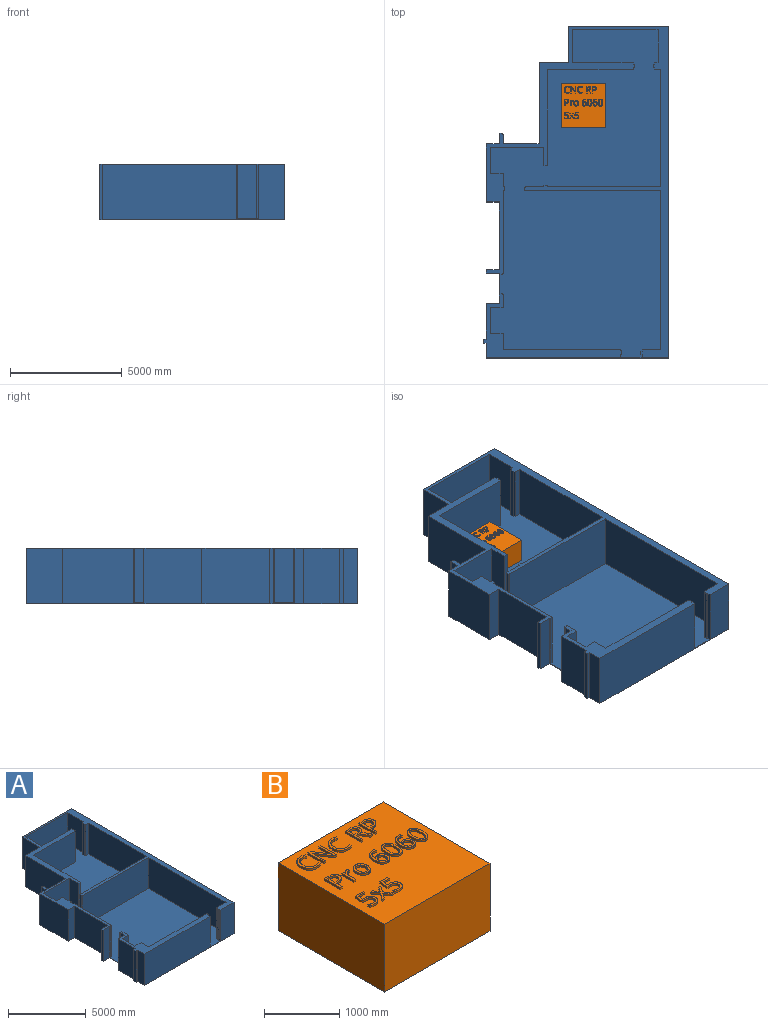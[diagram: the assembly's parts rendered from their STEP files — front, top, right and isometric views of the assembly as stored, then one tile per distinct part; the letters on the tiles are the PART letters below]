
ASSEMBLY  parts=2 mates=1
PART A: 99 faces, bbox 8276.1x14831.1x2468.9 mm
  f0: plane 14664.87x7617.86mm, normal (0,0,1), area 87596597.3mm2, adj f1,f13,f14,f22,f23,f24,f25,f26
  f1: plane 8150.75x2468.88mm, normal (0,-1,0), area 17745459.7mm2, adj f0,f2,f20,f21,f22,f38,f97,f98
  f2: plane 14831.13x2468.88mm, normal (1,0,0), area 36616275.6mm2, adj f1,f3,f21,f98
  f3: plane 4488.1x2468.88mm, normal (0,1,0), area 11080584.4mm2, adj f2,f4,f21,f98
  f4: plane 2468.88x1621.95mm, normal (-1,0,0), area 4004402.6mm2, adj f3,f5,f21,f98
  f5: plane 2468.88x1301.63mm, normal (0,1,0), area 3213578.3mm2, adj f4,f6,f21,f98
  f6: plane 3647.91x2468.88mm, normal (-1,0,0), area 9006245.3mm2, adj f5,f7,f21,f98
  f7: plane 2468.88x2348.04mm, normal (0,1,0), area 5391615mm2, adj f6,f8,f21,f39,f40,f46,f98
  f8: plane 2590.65x2468.88mm, normal (-1,0,0), area 6395991.8mm2, adj f7,f9,f21,f98
  f9: plane 2468.88x577.86mm, normal (0,-1,0), area 1426664.6mm2, adj f8,f10,f21,f98
  f10: plane 3026.45x2468.88mm, normal (-1,0,0), area 7471946.9mm2, adj f9,f11,f21,f98
  f11: plane 2468.88x577.86mm, normal (0,1,0), area 1426664.6mm2, adj f10,f12,f21,f98
  f12: plane 2468.88x156.95mm, normal (-1,0,0), area 387486mm2, adj f11,f13,f21,f98
  f13: plane 2468.88x603.36mm, normal (0,-1,0), area 1488839.6mm2, adj f0,f12,f14,f21,f47,f98
  f14: plane 2468.88x1372.56mm, normal (-1,0,0), area 1021102.5mm2, adj f0,f13,f15,f21,f37,f38
  f15: plane 2468.88x586.51mm, normal (0,1,0), area 1448027.1mm2, adj f14,f16,f21,f38
  f16: plane 2468.88x1571.79mm, normal (-1,0,0), area 3880553.8mm2, adj f15,f17,f21,f38
  f17: plane 2468.88x129.53mm, normal (0,1,0), area 319783.6mm2, adj f16,f18,f21,f38
  f18: plane 2468.88x191.97mm, normal (-1,0,0), area 473943.5mm2, adj f17,f19,f21,f38
  f19: plane 2468.88x125.31mm, normal (0,-1,0), area 309366.7mm2, adj f18,f20,f21,f38
  f20: plane 2468.88x650.91mm, normal (-1,0,0), area 1607024.3mm2, adj f1,f19,f21,f38
  f21: plane 14831.13x8276.06mm, normal (0,0,-1), area 103714263.4mm2, adj f1,f2,f3,f4,f5,f6,f7,f8
  f22: plane 2438.4x173.04mm, normal (1,0,0), area 421945.8mm2, adj f0,f1,f23,f38
  f23: plane 2438.4x49.23mm, normal (0,-1,0), area 120036.9mm2, adj f0,f22,f24,f38
  f24: plane 2438.4x135.75mm, normal (1,0,0), area 331009.4mm2, adj f0,f23,f25,f38
  f25: plane 2438.4x37.29mm, normal (0,1,0), area 90924.1mm2, adj f0,f24,f26,f38
  f26: plane 2438.4x67.02mm, normal (1,0,0), area 163418mm2, adj f0,f25,f27,f38
  f27: plane 5244.59x2438.4mm, normal (0,1,0), area 12788415.3mm2, adj f0,f26,f28,f38
  f28: plane 2438.4x698.26mm, normal (1,0,0), area 1702637.3mm2, adj f0,f27,f29,f38
  f29: plane 2438.4x565.36mm, normal (0,1,0), area 1378581.8mm2, adj f0,f28,f30,f38
  f30: plane 2438.4x1164.09mm, normal (1,0,0), area 2838507mm2, adj f0,f29,f31,f38
  f31: plane 2438.4x565.36mm, normal (0,-1,0), area 1378581.8mm2, adj f0,f30,f32,f38
  f32: plane 2438.4x581.62mm, normal (1,0,0), area 1418221.9mm2, adj f0,f31,f33,f38
  f33: plane 2438.4x31.86mm, normal (0,1,0), area 77690.3mm2, adj f0,f32,f34,f38
  f34: plane 2438.4x41.25mm, normal (1,0,0), area 100572.6mm2, adj f0,f33,f35,f38
  f35: plane 2438.4x108.66mm, normal (0,1,0), area 264949.5mm2, adj f0,f34,f36,f38
  f36: plane 2438.4x44.75mm, normal (-1,0,0), area 109122.4mm2, adj f0,f35,f37,f38
  f37: plane 2438.4x25.61mm, normal (0,1,0), area 62436.6mm2, adj f0,f14,f36,f38
  f38: plane 6164.04x2861.02mm, normal (0,0,1), area 3232495.8mm2, adj f1,f14,f15,f16,f17,f18,f19,f20
  f39: plane 466.68x166.26mm, normal (0,0,-1), area 75215.3mm2, adj f7,f40,f41,f42,f43,f44,f45,f46
  f40: plane 2438.4x429.05mm, normal (1,0,0), area 1046190.8mm2, adj f7,f39,f41,f98
  f41: plane 2438.4x37.63mm, normal (0,1,0), area 91762.1mm2, adj f39,f40,f42,f98
  f42: plane 2438.4x37.63mm, normal (1,0,0), area 91761.8mm2, adj f39,f41,f43,f98
  f43: plane 2438.4x103.13mm, normal (0,1,0), area 251472.7mm2, adj f39,f42,f44,f98
  f44: plane 2438.4x37.63mm, normal (-1,0,0), area 91761.8mm2, adj f39,f43,f45,f98
  f45: plane 2438.4x25.5mm, normal (0,1,0), area 62178.2mm2, adj f39,f44,f46,f98
  f46: plane 2438.4x429.05mm, normal (-1,0,0), area 1046190.8mm2, adj f7,f39,f45,f98
  f47: plane 2438.4x46.41mm, normal (-1,0,0), area 113171.5mm2, adj f0,f13,f48,f98
  f48: plane 2438.4x103.37mm, normal (0,-1,0), area 252064mm2, adj f0,f47,f49,f98
  f49: plane 2438.4x44.3mm, normal (1,0,0), area 108027.3mm2, adj f0,f48,f50,f98
  f50: plane 2438.4x37.15mm, normal (0,-1,0), area 90575.9mm2, adj f0,f49,f51,f98
  f51: plane 3677.29x2438.4mm, normal (1,0,0), area 8966714.5mm2, adj f0,f50,f52,f98
  f52: plane 2438.4x61.68mm, normal (0,-1,0), area 150402.7mm2, adj f0,f51,f53,f98
  f53: plane 2438.4x182.72mm, normal (1,0,0), area 445546.1mm2, adj f0,f52,f54,f98
  f54: plane 2438.4x58.49mm, normal (0,1,0), area 142625.9mm2, adj f0,f53,f55,f98
  f55: plane 2438.4x586.03mm, normal (1,0,0), area 1428964.5mm2, adj f0,f54,f56,f98
  f56: plane 2438.4x571.23mm, normal (0,1,0), area 1392877.5mm2, adj f0,f55,f57,f98
  f57: plane 2438.4x1177.99mm, normal (1,0,0), area 2872409.6mm2, adj f0,f56,f58,f98
  f58: plane 2438.4x2388.44mm, normal (0,-1,0), area 5823964mm2, adj f0,f57,f59,f98
  f59: plane 2438.4x800.31mm, normal (-1,0,0), area 1951472.7mm2, adj f0,f58,f60,f98
  f60: plane 2438.4x173.35mm, normal (0,-1,0), area 422690.5mm2, adj f0,f59,f61,f98
  f61: plane 4263.95x2438.4mm, normal (1,0,0), area 10397204.9mm2, adj f0,f60,f62,f98
  f62: plane 3816.53x2438.4mm, normal (0,-1,0), area 9306235.4mm2, adj f0,f61,f63,f98
  f63: plane 2438.4x99.27mm, normal (1,0,0), area 242066.6mm2, adj f0,f62,f64,f98
  f64: plane 2438.4x49.67mm, normal (0,-1,0), area 121119.4mm2, adj f0,f63,f65,f98
  f65: plane 2438.4x156.11mm, normal (1,0,0), area 380662.8mm2, adj f0,f64,f66,f98
  f66: plane 2438.4x49.67mm, normal (0,1,0), area 121119.4mm2, adj f0,f65,f67,f98
  f67: plane 2438.4x81.01mm, normal (1,0,0), area 197536.8mm2, adj f0,f66,f68,f98
  f68: plane 2718.1x2438.4mm, normal (0,1,0), area 6627812.9mm2, adj f0,f67,f69,f98
  f69: plane 2438.4x1455.69mm, normal (1,0,0), area 3549555.4mm2, adj f0,f68,f70,f98
  f70: plane 3828.21x2438.4mm, normal (0,-1,0), area 9334704.6mm2, adj f0,f69,f71,f98
  f71: plane 2438.4x1462.38mm, normal (-1,0,0), area 3565873mm2, adj f0,f70,f72,f98
  f72: plane 2438.4x145.51mm, normal (0,1,0), area 354813.2mm2, adj f0,f71,f73,f98
  f73: plane 2438.4x74.32mm, normal (-1,0,0), area 181219.2mm2, adj f0,f72,f74,f98
  f74: plane 2438.4x50.83mm, normal (0,1,0), area 123950.6mm2, adj f0,f73,f75,f98
  f75: plane 2438.4x160.46mm, normal (-1,0,0), area 391262.2mm2, adj f0,f74,f76,f98
  f76: plane 2438.4x50.83mm, normal (0,-1,0), area 123950.6mm2, adj f0,f75,f77,f98
  f77: plane 2438.4x81.33mm, normal (-1,0,0), area 198320.5mm2, adj f0,f76,f78,f98
  f78: plane 2438.4x274.95mm, normal (0,-1,0), area 670431.2mm2, adj f0,f77,f79,f98
  f79: plane 5241.25x2438.4mm, normal (-1,0,0), area 12780253mm2, adj f0,f78,f80,f98
  f80: plane 5055.05x2438.4mm, normal (0,1,0), area 12326241.8mm2, adj f0,f79,f81,f98
  f81: plane 2438.4x45.1mm, normal (1,0,0), area 109968.3mm2, adj f0,f80,f82,f98
  f82: plane 2438.4x174.05mm, normal (0,1,0), area 424393.3mm2, adj f0,f81,f83,f98
  f83: plane 2438.4x45.1mm, normal (-1,0,0), area 109968.3mm2, adj f0,f82,f84,f98
  f84: plane 2438.4x813.8mm, normal (0,1,0), area 1984361.4mm2, adj f0,f83,f85,f98
  f85: plane 2438.4x9.07mm, normal (-1,0,0), area 22106.8mm2, adj f0,f84,f86,f98
  f86: plane 2438.4x39.18mm, normal (0,1,0), area 95532mm2, adj f0,f85,f87,f98
  f87: plane 2438.4x143mm, normal (-1,0,0), area 348695.6mm2, adj f0,f86,f88,f98
  f88: plane 2438.4x39.18mm, normal (0,-1,0), area 95532mm2, adj f0,f87,f89,f98
  f89: plane 2438.4x30.65mm, normal (-1,0,0), area 74743.8mm2, adj f0,f88,f90,f98
  f90: plane 6036.43x2438.4mm, normal (0,-1,0), area 14719237mm2, adj f0,f89,f91,f98
  f91: plane 7086.6x2438.4mm, normal (-1,0,0), area 17279965.4mm2, adj f0,f90,f92,f98
  f92: plane 2438.4x833.23mm, normal (0,1,0), area 2031756.8mm2, adj f0,f91,f93,f98
  f93: plane 2438.4x75.93mm, normal (-1,0,0), area 185138.2mm2, adj f0,f92,f94,f98
  f94: plane 2438.4x53.7mm, normal (0,1,0), area 130949mm2, adj f0,f93,f95,f98
  f95: plane 2438.4x152.9mm, normal (-1,0,0), area 372840.6mm2, adj f0,f94,f96,f98
  f96: plane 2438.4x51.36mm, normal (0,-1,0), area 125241mm2, adj f0,f95,f97,f98
  f97: plane 2438.4x146.98mm, normal (-1,0,0), area 358394.4mm2, adj f0,f1,f96,f98
  f98: plane 14831.13x8137.78mm, normal (0,0,1), area 12960385.6mm2, adj f1,f2,f3,f4,f5,f6,f7,f8
PART B: 284 faces, bbox 1981.2x2000.3x1132.2 mm
  f0: plane 2000.25x1981.2mm, normal (0,0,1), area 3493503.6mm2, adj f1,f2,f3,f4,f6,f7,f8,f9
  f1: plane 1981.2x1101.73mm, normal (0,1,0), area 2182737.6mm2, adj f0,f2,f4,f5
  f2: plane 2000.25x1101.73mm, normal (-1,0,0), area 2203725.4mm2, adj f0,f1,f3,f5
  f3: plane 1981.2x1101.73mm, normal (0,-1,0), area 2182737.6mm2, adj f0,f2,f4,f5
  f4: plane 2000.25x1101.73mm, normal (1,0,0), area 2203725.4mm2, adj f0,f1,f3,f5
  f5: plane 2000.25x1981.2mm, normal (0,0,-1), area 3962895.3mm2, adj f1,f2,f3,f4
  f6: extruded ~78.65x33.17mm, area 2688.6mm2, adj f0,f7,f20,f21
  f7: extruded ~68.66x30.48mm, area 2166.9mm2, adj f0,f6,f8,f21
  f8: plane 30.48x30.16mm, normal (0.9,-0.44,0), area 1025.2mm2, adj f0,f7,f9,f21
  f9: extruded ~83.08x30.48mm, area 2609.2mm2, adj f0,f8,f10,f21
  f10: extruded ~77.62x30.48mm, area 2464.4mm2, adj f0,f9,f11,f21
  f11: extruded ~54.14x50.44mm, area 2289.1mm2, adj f0,f10,f12,f21
  f12: extruded ~81.82x30.48mm, area 2573.1mm2, adj f0,f11,f13,f21
  f13: extruded ~115.16x36.28mm, area 3764.5mm2, adj f0,f12,f14,f21
  f14: extruded ~103.02x40.55mm, area 3482mm2, adj f0,f13,f15,f21
  f15: extruded ~77.52x30.48mm, area 2403mm2, adj f0,f14,f16,f21
  f16: plane 30.76x30.48mm, normal (1,0,0), area 937.5mm2, adj f0,f15,f17,f21
  f17: extruded ~72.17x30.48mm, area 2233.6mm2, adj f0,f16,f18,f21
  f18: extruded ~79.28x32.38mm, area 2697.9mm2, adj f0,f17,f19,f21
  f19: extruded ~91.65x30.48mm, area 2982mm2, adj f0,f18,f20,f21
  f20: extruded ~90.85x30.48mm, area 2969.8mm2, adj f0,f6,f19,f21
  f21: plane 310.69x228.6mm, normal (0,0,1), area 19972.9mm2, adj f6,f7,f8,f9,f10,f11,f12,f13
  f22: plane 40.08x30.48mm, normal (0,-1,0), area 1221.8mm2, adj f0,f23,f36,f37
  f23: plane 302.22x30.48mm, normal (1,0,0), area 9211.7mm2, adj f0,f22,f24,f37
  f24: plane 32.87x30.48mm, normal (0,1,0), area 1002mm2, adj f0,f23,f25,f37
  f25: plane 173.43x30.48mm, normal (-1,0,0), area 5286.3mm2, adj f0,f24,f26,f37
  f26: extruded ~43.33x30.48mm, area 1321.2mm2, adj f0,f25,f27,f37
  f27: extruded ~35.85x30.48mm, area 1094.2mm2, adj f0,f26,f28,f37
  f28: plane 30.48x1.65mm, normal (0,1,0), area 50.4mm2, adj f0,f27,f29,f37
  f29: plane 252.61x164.77mm, normal (0.84,0.55,0), area 9192.7mm2, adj f0,f28,f30,f37
  f30: plane 39.69x30.48mm, normal (0,1,0), area 1209.7mm2, adj f0,f29,f31,f37
  f31: plane 302.22x30.48mm, normal (-1,0,0), area 9211.7mm2, adj f0,f30,f32,f37
  f32: plane 32.48x30.48mm, normal (0,-1,0), area 989.9mm2, adj f0,f31,f33,f37
  f33: plane 171.78x30.48mm, normal (1,0,0), area 5235.9mm2, adj f0,f32,f34,f37
  f34: extruded ~81.82x30.48mm, area 2496.5mm2, adj f0,f33,f35,f37
  f35: plane 30.48x1.65mm, normal (0,-1,0), area 50.4mm2, adj f0,f34,f36,f37
  f36: plane 253.6x165.17mm, normal (-0.84,-0.55,0), area 9224.6mm2, adj f0,f22,f35,f37
  f37: plane 302.22x236.07mm, normal (0,0,1), area 30152mm2, adj f22,f23,f24,f25,f26,f27,f28,f29
  f38: extruded ~78.65x33.17mm, area 2688.6mm2, adj f0,f39,f52,f53
  f39: extruded ~68.66x30.48mm, area 2166.9mm2, adj f0,f38,f40,f53
  f40: plane 30.48x30.16mm, normal (0.9,-0.44,0), area 1025.2mm2, adj f0,f39,f41,f53
  f41: extruded ~83.08x30.48mm, area 2609.2mm2, adj f0,f40,f42,f53
  f42: extruded ~77.62x30.48mm, area 2464.4mm2, adj f0,f41,f43,f53
  f43: extruded ~54.14x50.44mm, area 2289.1mm2, adj f0,f42,f44,f53
  f44: extruded ~81.82x30.48mm, area 2573.1mm2, adj f0,f43,f45,f53
  f45: extruded ~115.16x36.28mm, area 3764.5mm2, adj f0,f44,f46,f53
  f46: extruded ~103.02x40.55mm, area 3482mm2, adj f0,f45,f47,f53
  f47: extruded ~77.52x30.48mm, area 2403mm2, adj f0,f46,f48,f53
  f48: plane 30.76x30.48mm, normal (1,0,0), area 937.5mm2, adj f0,f47,f49,f53
  f49: extruded ~72.17x30.48mm, area 2233.6mm2, adj f0,f48,f50,f53
  f50: extruded ~79.28x32.38mm, area 2697.9mm2, adj f0,f49,f51,f53
  f51: extruded ~91.65x30.48mm, area 2982mm2, adj f0,f50,f52,f53
  f52: extruded ~90.85x30.48mm, area 2969.8mm2, adj f0,f38,f51,f53
  f53: plane 310.69x228.6mm, normal (0,0,1), area 19972.9mm2, adj f38,f39,f40,f41,f42,f43,f44,f45
  f54: plane 48.22x30.48mm, normal (0,1,0), area 1469.8mm2, adj f55,f71,f72,f73
  f55: plane 115.56x30.48mm, normal (1,0,0), area 3522.2mm2, adj f54,f56,f72,f73
  f56: plane 45.71x30.48mm, normal (0,-1,0), area 1393.1mm2, adj f55,f57,f72,f73
  f57: extruded ~56.75x30.48mm, area 1804.8mm2, adj f56,f58,f72,f73
  f58: extruded ~43.19x30.48mm, area 1477.5mm2, adj f57,f59,f72,f73
  f59: extruded ~44.35x30.48mm, area 1500.5mm2, adj f58,f71,f72,f73
  f60: plane 125.68x30.48mm, normal (1,0,0), area 3830.6mm2, adj f0,f61,f70,f72
  f61: plane 63.1x30.48mm, normal (0,-1,0), area 1923.4mm2, adj f0,f60,f62,f72
  f62: plane 125.68x73.16mm, normal (-0.86,-0.5,0), area 4432.4mm2, adj f0,f61,f63,f72
  f63: plane 41.54x30.48mm, normal (0,-1,0), area 1266.1mm2, adj f0,f62,f64,f72
  f64: plane 135.8x82.09mm, normal (0.86,0.52,0), area 4836.6mm2, adj f0,f63,f65,f72
  f65: extruded ~81.03x60.79mm, area 3330.5mm2, adj f0,f64,f66,f72
  f66: extruded ~64.1x30.48mm, area 2191.6mm2, adj f0,f65,f67,f72
  f67: extruded ~82.19x30.48mm, area 2635.6mm2, adj f0,f66,f68,f72
  f68: plane 82.88x30.48mm, normal (0,1,0), area 2526.2mm2, adj f0,f67,f69,f72
  f69: plane 302.22x30.48mm, normal (-1,0,0), area 9211.7mm2, adj f0,f68,f70,f72
  f70: plane 35.12x30.48mm, normal (0,-1,0), area 1070.6mm2, adj f0,f60,f69,f72
  f71: extruded ~54.54x30.48mm, area 1757.1mm2, adj f54,f59,f72,f73
  f72: plane 302.22x212.92mm, normal (0,0,1), area 27388.6mm2, adj f54,f55,f56,f57,f58,f59,f60,f61
  f73: plane 120.12x115.56mm, normal (0,0,1), area 12548.6mm2, adj f54,f55,f56,f57,f58,f59,f71
  f74: plane 31.68x30.48mm, normal (0,1,0), area 965.7mm2, adj f75,f88,f89,f90
  f75: plane 122.77x30.48mm, normal (1,0,0), area 3741.9mm2, adj f74,f76,f89,f90
  f76: plane 39.29x30.48mm, normal (0,-1,0), area 1197.6mm2, adj f75,f77,f89,f90
  f77: extruded ~61.19x30.48mm, area 1948.8mm2, adj f76,f78,f89,f90
  f78: extruded ~44.62x30.48mm, area 1545mm2, adj f77,f79,f89,f90
  f79: extruded ~48.42x30.48mm, area 1672.7mm2, adj f78,f88,f89,f90
  f80: extruded ~70.61x31.32mm, area 2443mm2, adj f0,f81,f87,f89
  f81: extruded ~113.24x88.04mm, area 4994.7mm2, adj f0,f80,f82,f89
  f82: plane 78.38x30.48mm, normal (0,1,0), area 2389.1mm2, adj f0,f81,f83,f89
  f83: plane 302.22x30.48mm, normal (-1,0,0), area 9211.7mm2, adj f0,f82,f84,f89
  f84: plane 35.12x30.48mm, normal (0,-1,0), area 1070.6mm2, adj f0,f83,f85,f89
  f85: plane 118.86x30.48mm, normal (1,0,0), area 3623mm2, adj f0,f84,f86,f89
  f86: plane 35.59x30.48mm, normal (0,-1,0), area 1084.7mm2, adj f0,f85,f87,f89
  f87: extruded ~89.59x30.48mm, area 2885.6mm2, adj f0,f80,f86,f89
  f88: extruded ~67.57x30.48mm, area 2141.9mm2, adj f74,f79,f89,f90
  f89: plane 302.22x191.62mm, normal (0,0,1), area 22512.9mm2, adj f74,f75,f76,f77,f78,f79,f80,f81
  f90: plane 122.77x120.12mm, normal (0,0,1), area 13108.8mm2, adj f74,f75,f76,f77,f78,f79,f88
  f91: plane 31.68x30.48mm, normal (0,1,0), area 965.7mm2, adj f92,f105,f106,f107
  f92: plane 122.77x30.48mm, normal (1,0,0), area 3741.9mm2, adj f91,f93,f106,f107
  f93: plane 39.29x30.48mm, normal (0,-1,0), area 1197.6mm2, adj f92,f94,f106,f107
  f94: extruded ~61.19x30.48mm, area 1948.8mm2, adj f93,f95,f106,f107
  f95: extruded ~44.62x30.48mm, area 1545mm2, adj f94,f96,f106,f107
  f96: extruded ~48.42x30.48mm, area 1672.7mm2, adj f95,f105,f106,f107
  f97: extruded ~70.61x31.32mm, area 2443mm2, adj f0,f98,f104,f106
  f98: extruded ~113.24x88.04mm, area 4994.7mm2, adj f0,f97,f99,f106
  f99: plane 78.38x30.48mm, normal (0,1,0), area 2389.1mm2, adj f0,f98,f100,f106
  f100: plane 302.22x30.48mm, normal (-1,0,0), area 9211.7mm2, adj f0,f99,f101,f106
  f101: plane 35.12x30.48mm, normal (0,-1,0), area 1070.6mm2, adj f0,f100,f102,f106
  f102: plane 118.86x30.48mm, normal (1,0,0), area 3623mm2, adj f0,f101,f103,f106
  f103: plane 35.59x30.48mm, normal (0,-1,0), area 1084.7mm2, adj f0,f102,f104,f106
  f104: extruded ~89.59x30.48mm, area 2885.6mm2, adj f0,f97,f103,f106
  f105: extruded ~67.57x30.48mm, area 2141.9mm2, adj f91,f96,f106,f107
  f106: plane 302.22x191.62mm, normal (0,0,1), area 22512.9mm2, adj f91,f92,f93,f94,f95,f96,f97,f98
  f107: plane 122.77x120.12mm, normal (0,0,1), area 13108.8mm2, adj f91,f92,f93,f94,f95,f96,f105
  f108: extruded ~30.48x27.05mm, area 829.6mm2, adj f0,f109,f120,f121
  f109: extruded ~39.09x30.48mm, area 1265.6mm2, adj f0,f108,f110,f121
  f110: extruded ~34.1x30.48mm, area 1404.1mm2, adj f0,f109,f111,f121
  f111: plane 30.48x1.65mm, normal (0,1,0), area 50.4mm2, adj f0,f110,f112,f121
  f112: plane 41.94x30.48mm, normal (1,0.09,0), area 1283.9mm2, adj f0,f111,f113,f121
  f113: plane 30.48x28.31mm, normal (0,1,0), area 862.9mm2, adj f0,f112,f114,f121
  f114: plane 226.55x30.48mm, normal (-1,0,0), area 6905.2mm2, adj f0,f113,f115,f121
  f115: plane 34.33x30.48mm, normal (0,-1,0), area 1046.4mm2, adj f0,f114,f116,f121
  f116: plane 121.58x30.48mm, normal (1,0,0), area 3705.6mm2, adj f0,f115,f117,f121
  f117: extruded ~55.6x30.48mm, area 1837mm2, adj f0,f116,f118,f121
  f118: extruded ~47.03x30.48mm, area 1639.6mm2, adj f0,f117,f119,f121
  f119: extruded ~30.48x24.8mm, area 763.4mm2, adj f0,f118,f120,f121
  f120: plane 31.82x30.48mm, normal (0.99,-0.15,0), area 980.6mm2, adj f0,f108,f119,f121
  f121: plane 230.72x130.44mm, normal (0,0,1), area 10703.2mm2, adj f108,f109,f110,f111,f112,f113,f114,f115
  f122: extruded ~66.18x30.48mm, area 2122mm2, adj f123,f138,f139,f140
  f123: extruded ~65.91x30.48mm, area 2113.1mm2, adj f122,f124,f139,f140
  f124: extruded ~50.83x30.48mm, area 1754.2mm2, adj f123,f125,f139,f140
  f125: extruded ~51.59x30.48mm, area 1779.8mm2, adj f124,f126,f139,f140
  f126: extruded ~65.62x30.48mm, area 2107mm2, adj f125,f127,f139,f140
  f127: extruded ~66.28x30.48mm, area 2126.3mm2, adj f126,f128,f139,f140
  f128: extruded ~51.2x30.48mm, area 1771.6mm2, adj f127,f138,f139,f140
  f129: extruded ~86.55x30.48mm, area 2835.7mm2, adj f0,f130,f137,f139
  f130: extruded ~85.56x30.48mm, area 2807mm2, adj f0,f129,f131,f139
  f131: extruded ~75.51x31.65mm, area 2576.9mm2, adj f0,f130,f132,f139
  f132: extruded ~76.93x30.92mm, area 2607.8mm2, adj f0,f131,f133,f139
  f133: extruded ~86.29x30.48mm, area 2826.3mm2, adj f0,f132,f134,f139
  f134: extruded ~62.44x30.48mm, area 1959.5mm2, adj f0,f133,f135,f139
  f135: extruded ~40.94x36.38mm, area 1693.6mm2, adj f0,f134,f136,f139
  f136: extruded ~53.98x30.48mm, area 1723.7mm2, adj f0,f135,f137,f139
  f137: extruded ~77.09x31.12mm, area 2615.1mm2, adj f0,f129,f136,f139
  f138: extruded ~51.03x30.48mm, area 1768.9mm2, adj f122,f128,f139,f140
  f139: plane 234.88x208.16mm, normal (0,0,1), area 19714.7mm2, adj f122,f123,f124,f125,f126,f127,f128,f129
  f140: plane 176.94x137.05mm, normal (0,0,1), area 20118.4mm2, adj f122,f123,f124,f125,f126,f127,f128,f138
  f141: extruded ~45.57x30.48mm, area 1548.8mm2, adj f142,f165,f166,f167
  f142: extruded ~34.63x30.48mm, area 1123.5mm2, adj f141,f143,f166,f167
  f143: extruded ~30.48x29.14mm, area 1153.9mm2, adj f142,f144,f166,f167
  f144: extruded ~39.69x30.48mm, area 1245mm2, adj f143,f145,f166,f167
  f145: extruded ~30.48x27.91mm, area 909.8mm2, adj f144,f146,f166,f167
  f146: extruded ~30.48x24.71mm, area 1001.4mm2, adj f145,f147,f166,f167
  f147: extruded ~34.1x30.48mm, area 1074.9mm2, adj f146,f148,f166,f167
  f148: extruded ~45.05x30.48mm, area 1516.6mm2, adj f147,f149,f166,f167
  f149: extruded ~47.13x30.48mm, area 1542.3mm2, adj f148,f165,f166,f167
  f150: extruded ~133.22x34.63mm, area 4271.1mm2, adj f0,f151,f164,f166
  f151: extruded ~98.09x30.48mm, area 3162.6mm2, adj f0,f150,f152,f166
  f152: extruded ~74.38x35.26mm, area 2605.3mm2, adj f0,f151,f153,f166
  f153: extruded ~69.59x30.48mm, area 2341.9mm2, adj f0,f152,f154,f166
  f154: extruded ~74.15x30.48mm, area 2453.4mm2, adj f0,f153,f155,f166
  f155: extruded ~66.74x30.48mm, area 2211.4mm2, adj f0,f154,f156,f166
  f156: extruded ~64.19x30.48mm, area 2157.1mm2, adj f0,f155,f157,f166
  f157: extruded ~71.97x35.59mm, area 2563.2mm2, adj f0,f156,f158,f166
  f158: plane 30.48x2.45mm, normal (0,1,0), area 74.6mm2, adj f0,f157,f159,f166
  f159: extruded ~95.22x30.48mm, area 3079.7mm2, adj f0,f158,f160,f166
  f160: extruded ~74.25x30.48mm, area 2527.3mm2, adj f0,f159,f161,f166
  f161: extruded ~36.38x30.48mm, area 1124.5mm2, adj f0,f160,f162,f166
  f162: plane 30.48x29.57mm, normal (1,0,0), area 901.2mm2, adj f0,f161,f163,f166
  f163: extruded ~36.78x30.48mm, area 1130.7mm2, adj f0,f162,f164,f166
  f164: extruded ~102.43x44.12mm, area 3527mm2, adj f0,f150,f163,f166
  f165: extruded ~53.45x30.48mm, area 1739.7mm2, adj f141,f149,f166,f167
  f166: plane 310.69x197.18mm, normal (0,0,1), area 23635.5mm2, adj f141,f142,f143,f144,f145,f146,f147,f148
  f167: plane 136.26x128.12mm, normal (0,0,1), area 14076.4mm2, adj f141,f142,f143,f144,f145,f146,f147,f148
  f168: extruded ~96.04x30.48mm, area 2989.9mm2, adj f169,f183,f184,f185
  f169: extruded ~95.81x30.48mm, area 2983.1mm2, adj f168,f170,f184,f185
  f170: extruded ~49.38x30.48mm, area 1861.8mm2, adj f169,f171,f184,f185
  f171: extruded ~49.71x30.48mm, area 1880.2mm2, adj f170,f172,f184,f185
  f172: extruded ~95.38x30.48mm, area 2968.7mm2, adj f171,f173,f184,f185
  f173: extruded ~95.65x30.48mm, area 2976.5mm2, adj f172,f174,f184,f185
  f174: extruded ~49.71x30.49mm, area 1884.1mm2, adj f173,f183,f184,f185
  f175: extruded ~117.05x30.48mm, area 3692.3mm2, adj f0,f176,f182,f184
  f176: extruded ~115.52x30.48mm, area 3653mm2, adj f0,f175,f177,f184
  f177: extruded ~74.74x39.92mm, area 2706.5mm2, adj f0,f176,f178,f184
  f178: extruded ~75.01x38.27mm, area 2688.3mm2, adj f0,f177,f179,f184
  f179: extruded ~117.18x30.48mm, area 3695.8mm2, adj f0,f178,f180,f184
  f180: extruded ~116.12x30.48mm, area 3670.3mm2, adj f0,f179,f181,f184
  f181: extruded ~74.18x39.59mm, area 2685.1mm2, adj f0,f180,f182,f184
  f182: extruded ~75.57x38.66mm, area 2710.9mm2, adj f0,f175,f181,f184
  f183: extruded ~49.38x30.48mm, area 1866.3mm2, adj f168,f174,f184,f185
  f184: plane 311.15x199.89mm, normal (0,0,1), area 24120.8mm2, adj f168,f169,f170,f171,f172,f173,f174,f175
  f185: plane 251.82x129.98mm, normal (0,0,1), area 27639.4mm2, adj f168,f169,f170,f171,f172,f173,f174,f183
  f186: extruded ~45.57x30.48mm, area 1548.8mm2, adj f187,f210,f211,f212
  f187: extruded ~34.63x30.48mm, area 1123.5mm2, adj f186,f188,f211,f212
  f188: extruded ~30.48x29.14mm, area 1153.9mm2, adj f187,f189,f211,f212
  f189: extruded ~39.69x30.48mm, area 1245mm2, adj f188,f190,f211,f212
  f190: extruded ~30.48x27.91mm, area 909.8mm2, adj f189,f191,f211,f212
  f191: extruded ~30.48x24.71mm, area 1001.4mm2, adj f190,f192,f211,f212
  f192: extruded ~34.1x30.48mm, area 1074.9mm2, adj f191,f193,f211,f212
  f193: extruded ~45.05x30.48mm, area 1516.6mm2, adj f192,f194,f211,f212
  f194: extruded ~47.13x30.48mm, area 1542.3mm2, adj f193,f210,f211,f212
  f195: extruded ~133.22x34.63mm, area 4271.1mm2, adj f0,f196,f209,f211
  f196: extruded ~98.09x30.48mm, area 3162.6mm2, adj f0,f195,f197,f211
  f197: extruded ~74.38x35.26mm, area 2605.3mm2, adj f0,f196,f198,f211
  f198: extruded ~69.59x30.48mm, area 2341.9mm2, adj f0,f197,f199,f211
  f199: extruded ~74.15x30.48mm, area 2453.4mm2, adj f0,f198,f200,f211
  f200: extruded ~66.74x30.48mm, area 2211.4mm2, adj f0,f199,f201,f211
  f201: extruded ~64.19x30.48mm, area 2157.1mm2, adj f0,f200,f202,f211
  f202: extruded ~71.97x35.59mm, area 2563.2mm2, adj f0,f201,f203,f211
  f203: plane 30.48x2.45mm, normal (0,1,0), area 74.6mm2, adj f0,f202,f204,f211
  f204: extruded ~95.22x30.48mm, area 3079.7mm2, adj f0,f203,f205,f211
  f205: extruded ~74.25x30.48mm, area 2527.3mm2, adj f0,f204,f206,f211
  f206: extruded ~36.38x30.48mm, area 1124.5mm2, adj f0,f205,f207,f211
  f207: plane 30.48x29.57mm, normal (1,0,0), area 901.2mm2, adj f0,f206,f208,f211
  f208: extruded ~36.78x30.48mm, area 1130.7mm2, adj f0,f207,f209,f211
  f209: extruded ~102.43x44.12mm, area 3527mm2, adj f0,f195,f208,f211
  f210: extruded ~53.45x30.48mm, area 1739.7mm2, adj f186,f194,f211,f212
  f211: plane 310.69x197.18mm, normal (0,0,1), area 23635.5mm2, adj f186,f187,f188,f189,f190,f191,f192,f193
  f212: plane 136.26x128.12mm, normal (0,0,1), area 14076.4mm2, adj f186,f187,f188,f189,f190,f191,f192,f193
  f213: extruded ~96.04x30.48mm, area 2989.9mm2, adj f214,f228,f229,f230
  f214: extruded ~95.81x30.48mm, area 2983.1mm2, adj f213,f215,f229,f230
  f215: extruded ~49.38x30.48mm, area 1861.8mm2, adj f214,f216,f229,f230
  f216: extruded ~49.71x30.48mm, area 1880.2mm2, adj f215,f217,f229,f230
  f217: extruded ~95.38x30.48mm, area 2968.7mm2, adj f216,f218,f229,f230
  f218: extruded ~95.65x30.48mm, area 2976.5mm2, adj f217,f219,f229,f230
  f219: extruded ~49.71x30.49mm, area 1884.1mm2, adj f218,f228,f229,f230
  f220: extruded ~117.05x30.48mm, area 3692.3mm2, adj f0,f221,f227,f229
  f221: extruded ~115.52x30.48mm, area 3653mm2, adj f0,f220,f222,f229
  f222: extruded ~74.74x39.92mm, area 2706.5mm2, adj f0,f221,f223,f229
  f223: extruded ~75.01x38.27mm, area 2688.3mm2, adj f0,f222,f224,f229
  f224: extruded ~117.18x30.48mm, area 3695.8mm2, adj f0,f223,f225,f229
  f225: extruded ~116.12x30.48mm, area 3670.3mm2, adj f0,f224,f226,f229
  f226: extruded ~74.18x39.59mm, area 2685.1mm2, adj f0,f225,f227,f229
  f227: extruded ~75.57x38.66mm, area 2710.9mm2, adj f0,f220,f226,f229
  f228: extruded ~49.38x30.48mm, area 1866.3mm2, adj f213,f219,f229,f230
  f229: plane 311.15x199.89mm, normal (0,0,1), area 24120.8mm2, adj f213,f214,f215,f216,f217,f218,f219,f220
  f230: plane 251.82x129.98mm, normal (0,0,1), area 27639.4mm2, adj f213,f214,f215,f216,f217,f218,f219,f228
  f231: extruded ~75.14x30.48mm, area 2454.2mm2, adj f0,f232,f249,f250
  f232: extruded ~47.36x30.48mm, area 1453.2mm2, adj f0,f231,f233,f250
  f233: plane 90.75x30.48mm, normal (1,-0.08,0), area 2776mm2, adj f0,f232,f234,f250
  f234: plane 120.91x30.48mm, normal (0,-1,0), area 3685.5mm2, adj f0,f233,f235,f250
  f235: plane 31.62x30.48mm, normal (1,0,0), area 963.7mm2, adj f0,f234,f236,f250
  f236: plane 150.28x30.48mm, normal (0,1,0), area 4580.6mm2, adj f0,f235,f237,f250
  f237: plane 141.42x30.48mm, normal (-1,0.08,0), area 4324.4mm2, adj f0,f236,f238,f250
  f238: plane 30.48x17.79mm, normal (-0.54,-0.84,0), area 643.7mm2, adj f0,f237,f239,f250
  f239: extruded ~52.52x30.48mm, area 1613.3mm2, adj f0,f238,f240,f250
  f240: extruded ~77.46x63.24mm, area 3487.4mm2, adj f0,f239,f241,f250
  f241: extruded ~49.64x30.48mm, area 1688.2mm2, adj f0,f240,f242,f250
  f242: extruded ~56.52x30.48mm, area 1838.9mm2, adj f0,f241,f243,f250
  f243: extruded ~42.4x30.48mm, area 1305.5mm2, adj f0,f242,f244,f250
  f244: extruded ~35.92x30.48mm, area 1186.5mm2, adj f0,f243,f245,f250
  f245: plane 33.07x30.48mm, normal (-1,0,0), area 1008.1mm2, adj f0,f244,f246,f250
  f246: extruded ~77.92x30.48mm, area 2455.5mm2, adj f0,f245,f247,f250
  f247: extruded ~82.38x30.48mm, area 2700.6mm2, adj f0,f246,f248,f250
  f248: extruded ~73.59x30.48mm, area 2498.3mm2, adj f0,f247,f249,f250
  f249: extruded ~64.82x30.48mm, area 2217mm2, adj f0,f231,f248,f250
  f250: plane 306.39x190.17mm, normal (0,0,1), area 21197.9mm2, adj f231,f232,f233,f234,f235,f236,f237,f238
  f251: plane 110.6x78.78mm, normal (-0.81,-0.58,0), area 4138.7mm2, adj f0,f252,f262,f263
  f252: plane 115.95x82.88mm, normal (-0.81,0.58,0), area 4344.3mm2, adj f0,f251,f253,f263
  f253: plane 38.83x30.48mm, normal (0,-1,0), area 1183.5mm2, adj f0,f252,f254,f263
  f254: plane 91.81x64.1mm, normal (0.82,-0.57,0), area 3412.9mm2, adj f0,f253,f255,f263
  f255: plane 91.81x63.5mm, normal (-0.82,-0.57,0), area 3402.5mm2, adj f0,f254,f256,f263
  f256: plane 38.83x30.48mm, normal (0,-1,0), area 1183.5mm2, adj f0,f255,f257,f263
  f257: plane 115.95x82.88mm, normal (0.81,0.58,0), area 4344.3mm2, adj f0,f256,f258,f263
  f258: plane 110.6x78.78mm, normal (0.81,-0.58,0), area 4138.7mm2, adj f0,f257,f259,f263
  f259: plane 38.7x30.48mm, normal (0,1,0), area 1179.4mm2, adj f0,f258,f260,f263
  f260: plane 86.78x59.53mm, normal (-0.82,0.57,0), area 3207.7mm2, adj f0,f259,f261,f263
  f261: plane 86.78x59.73mm, normal (0.82,0.57,0), area 3211.1mm2, adj f0,f260,f262,f263
  f262: plane 39.09x30.48mm, normal (0,1,0), area 1191.5mm2, adj f0,f251,f261,f263
  f263: plane 226.55x205.25mm, normal (0,0,1), area 16237mm2, adj f251,f252,f253,f254,f255,f256,f257,f258
  f264: extruded ~75.14x30.48mm, area 2454.2mm2, adj f0,f265,f282,f283
  f265: extruded ~47.36x30.48mm, area 1453.2mm2, adj f0,f264,f266,f283
  f266: plane 90.75x30.48mm, normal (1,-0.08,0), area 2776mm2, adj f0,f265,f267,f283
  f267: plane 120.91x30.48mm, normal (0,-1,0), area 3685.5mm2, adj f0,f266,f268,f283
  f268: plane 31.62x30.48mm, normal (1,0,0), area 963.7mm2, adj f0,f267,f269,f283
  f269: plane 150.28x30.48mm, normal (0,1,0), area 4580.6mm2, adj f0,f268,f270,f283
  f270: plane 141.42x30.48mm, normal (-1,0.08,0), area 4324.4mm2, adj f0,f269,f271,f283
  f271: plane 30.48x17.79mm, normal (-0.54,-0.84,0), area 643.7mm2, adj f0,f270,f272,f283
  f272: extruded ~52.52x30.48mm, area 1613.3mm2, adj f0,f271,f273,f283
  f273: extruded ~77.46x63.24mm, area 3487.4mm2, adj f0,f272,f274,f283
  f274: extruded ~49.64x30.48mm, area 1688.2mm2, adj f0,f273,f275,f283
  f275: extruded ~56.52x30.48mm, area 1838.9mm2, adj f0,f274,f276,f283
  f276: extruded ~42.4x30.48mm, area 1305.5mm2, adj f0,f275,f277,f283
  f277: extruded ~35.92x30.48mm, area 1186.5mm2, adj f0,f276,f278,f283
  f278: plane 33.07x30.48mm, normal (-1,0,0), area 1008.1mm2, adj f0,f277,f279,f283
  f279: extruded ~77.92x30.48mm, area 2455.5mm2, adj f0,f278,f280,f283
  f280: extruded ~82.38x30.48mm, area 2700.6mm2, adj f0,f279,f281,f283
  f281: extruded ~73.59x30.48mm, area 2498.3mm2, adj f0,f280,f282,f283
  f282: extruded ~64.82x30.48mm, area 2217mm2, adj f0,f264,f281,f283
  f283: plane 306.39x190.17mm, normal (0,0,1), area 21197.9mm2, adj f264,f265,f266,f267,f268,f269,f270,f271
PLACE A at identity fixed
PLACE B t=(5363.07,7270.59,0)mm
MATE planar B.f5 <-> A.f0  axis (0,0,-1) through (5363.07,7270.59,0)mm
